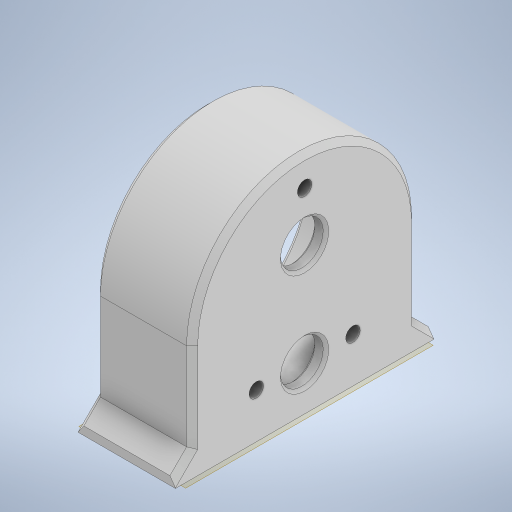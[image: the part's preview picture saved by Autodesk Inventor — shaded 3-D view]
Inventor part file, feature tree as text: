
AUTODESK INVENTOR PART (.ipt)
format: ipt  version: 2024 (Build 280153000, 153)  size: 308,224 bytes
history: native  units: in
note: dims shown in document units (in); Inventor stores cm internally (conversion verified against a paired STEP export)
features: extrude x4, sketch x4, chamfer x3, plane x1
ambient origin geometry x8: Origin, YZ Plane, XZ Plane, XY Plane, X Axis, Y Axis, Z Axis, Center Point
bodies: Solid1 (feature_tree)
feature tree (12):
  extrude  "Extrusion1"  Depth=1.5945in
  extrude  "Extrusion2"  Depth=0.3031in
  plane  "Work Plane1"
  extrude  "Extrusion3"  Depth=0.4862in
  extrude  "Extrusion4"  Depth=0.0197in
  chamfer  "Chamfer1"  Distance=0.1024in
  chamfer  "Chamfer2"  Distance=0.5886in
  chamfer  "Chamfer3"  Distance=0.685in
  sketch  "Sketch1"  dims[d0=1.5945in d1=1.3583in]
  sketch  "Sketch2"  dims[d2=0.3031in d3=0.3031in]
  sketch  "Sketch3"  dims[d4=0.2402in d5=0.4862in]
  sketch  "Sketch4"  dims[d6=0.1024in d7=0.1024in d8=0.1024in d9=0.5886in d10=0.685in d12=0.3425in d13=0.4787in d14=0.0984in d15=0.0in d16=1.3583in d17=0.5906in d18=0.0in d19=0.3937in d20=0.0in d21=0.1181in d22=0.1181in d23=0.1181in d24=0.0in d25=0.0591in d26=0.0787in d27=45.0deg d28=0.0394in d29=0.0787in d30=45.0deg d31=0.0197in d32=0.0787in d33=45.0deg]
